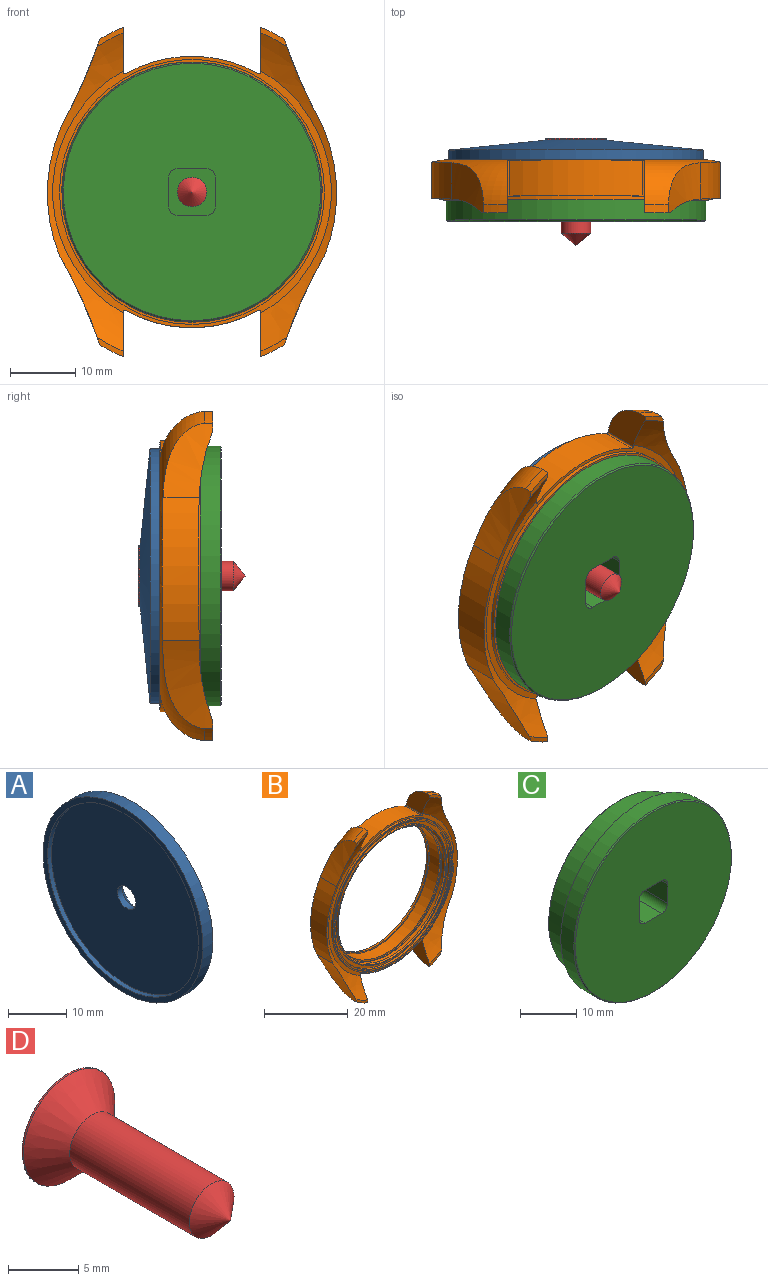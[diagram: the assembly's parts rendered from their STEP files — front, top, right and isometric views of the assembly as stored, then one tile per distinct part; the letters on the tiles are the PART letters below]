
ASSEMBLY  parts=4 mates=3
PART A: 7 faces, bbox 4x38.9x38.9 mm
  f0: cone r=19.47mm half-angle=84.2deg, axis (-1,0,0), area 1141.1mm2, adj f1,f6
  f1: cylinder r=19.47mm len=38.95mm, axis (-1,0,0), area 297.3mm2, adj f0,f2
  f2: plane 38.95x38.95mm, normal (-1,0,0), area 130.5mm2, adj f1,f3
  f3: cylinder r=18.38mm len=36.75mm, axis (-1,0,0), area 107.4mm2, adj f2,f4
  f4: plane 36.75x36.75mm, normal (-1,0,0), area 1044.8mm2, adj f3,f5
  f5: cylinder r=2.25mm len=4.5mm, axis (-1,0,0), area 17.6mm2, adj f4,f6
  f6: bspline ~8.47x8.47mm, area 54.6mm2, adj f0,f5
PART B: 52 faces, bbox 59.5x8.5x59.5 mm
  f0: cylinder r=27.3mm len=3.62mm, axis (0,-1,0), area 5mm2, adj f6,f9,f38,f46
  f1: cylinder r=27.3mm len=3.62mm, axis (0,-1,0), area 5mm2, adj f9,f35,f41,f44
  f2: plane 4x2.97mm, normal (0,-1,0), area 3.3mm2, adj f5,f7,f39,f45
  f3: plane 4x2.97mm, normal (0,-1,0), area 3.3mm2, adj f8,f34,f36,f43
  f4: plane 42.6x41.5mm, normal (0,-1,0), area 113mm2, adj f5,f33,f34,f36,f37,f38,f39,f40
  f5: torus R=10.97mm, axis (0,-1,0), area 113mm2, adj f2,f4,f6,f38,f39,f45,f46,f47
  f6: plane 4x2.97mm, normal (0,-1,0), area 3.3mm2, adj f0,f5,f38,f46
  f7: cylinder r=27.3mm len=3.62mm, axis (0,-1,0), area 5mm2, adj f2,f9,f39,f45
  f8: cylinder r=27.3mm len=3.62mm, axis (0,-1,0), area 5mm2, adj f3,f9,f36,f43
  f9: torus R=19.83mm, axis (0,-1,0), area 417.3mm2, adj f0,f1,f7,f8,f10,f36,f37,f38
  f10: plane 40.38x40.38mm, normal (0,1,0), area 90.5mm2, adj f9,f11
  f11: cylinder r=19.46mm len=38.93mm, axis (0,-1,0), area 137.6mm2, adj f10,f12
  f12: plane 38.93x38.93mm, normal (0,1,0), area 92.9mm2, adj f11,f13
  f13: cylinder r=18.69mm len=37.38mm, axis (0,-1,0), area 23.5mm2, adj f12,f14
  f14: plane 37.38x37.38mm, normal (0,1,0), area 49.2mm2, adj f13,f15
  f15: cone r=18.35mm half-angle=30deg, axis (0,1,0), area 19.9mm2, adj f14,f16
  f16: cylinder r=18.35mm len=36.7mm, axis (0,-1,0), area 89.4mm2, adj f15,f17
  f17: plane 36.7x36.7mm, normal (0,1,0), area 94.9mm2, adj f16,f18
  f18: cylinder r=17.51mm len=35.02mm, axis (0,-1,0), area 66mm2, adj f17,f19
  f19: plane 35.72x35.72mm, normal (0,-1,0), area 38.9mm2, adj f18,f20
  f20: cylinder r=17.86mm len=35.72mm, axis (0,-1,0), area 387.1mm2, adj f19,f21
  f21: plane 36.6x36.6mm, normal (0,-1,0), area 50.3mm2, adj f20,f22
  f22: cylinder r=18.3mm len=36.6mm, axis (0,-1,0), area 34.5mm2, adj f21,f23
  f23: cone r=18.3mm half-angle=43.3deg, axis (0,1,0), area 47.9mm2, adj f22,f24
  f24: cylinder r=18.01mm len=36.03mm, axis (0,-1,0), area 100.6mm2, adj f23,f25
  f25: cone r=18.3mm half-angle=43.3deg, axis (0,-1,0), area 47.9mm2, adj f24,f26
  f26: plane 37.03x37.03mm, normal (0,-1,0), area 24.6mm2, adj f25,f27
  f27: cylinder r=18.51mm len=37.03mm, axis (0,-1,0), area 65.7mm2, adj f26,f28
  f28: plane 39x39mm, normal (0,-1,0), area 117.6mm2, adj f27,f29
  f29: cylinder r=19.5mm len=39mm, axis (0,-1,0), area 75.3mm2, adj f28,f30
  f30: plane 39.83x39.83mm, normal (0,-1,0), area 51.4mm2, adj f29,f31
  f31: cylinder r=19.91mm len=39.83mm, axis (0,-1,0), area 31.3mm2, adj f30,f32
  f32: plane 40.5x40.5mm, normal (0,-1,0), area 42.6mm2, adj f31,f33
  f33: cylinder r=20.25mm len=40.5mm, axis (0,-1,0), area 76.3mm2, adj f4,f32
  f34: torus R=10.97mm, axis (0,-1,0), area 113mm2, adj f3,f4,f35,f36,f41,f42,f43,f44
  f35: plane 4x2.97mm, normal (0,-1,0), area 3.3mm2, adj f1,f34,f41,f44
  f36: plane 8.38x7.32mm, normal (-1,0,0), area 34.6mm2, adj f3,f4,f8,f9,f34,f48
  f37: cylinder r=20.75mm len=20.4mm, axis (0,1,0), area 117.4mm2, adj f4,f9,f48,f49
  f38: plane 8.38x7.32mm, normal (1,0,0), area 34.6mm2, adj f0,f4,f5,f6,f9,f49
  f39: plane 8.38x7.32mm, normal (1,0,0), area 34.6mm2, adj f2,f4,f5,f7,f9,f51
  f40: cylinder r=20.75mm len=20.4mm, axis (0,1,0), area 117.4mm2, adj f4,f9,f50,f51
  f41: plane 8.38x7.32mm, normal (-1,0,0), area 34.6mm2, adj f1,f4,f9,f34,f35,f50
  f42: cylinder r=25.39mm len=21.88mm, axis (0,1,0), area 125.6mm2, adj f9,f34,f43,f44
  f43: cylinder r=67.35mm len=13.52mm, axis (0,1,0), area 76.4mm2, adj f3,f8,f9,f34,f42
  f44: cylinder r=67.35mm len=11.33mm, axis (0,1,0), area 62.4mm2, adj f1,f9,f34,f35,f42
  f45: cylinder r=67.35mm len=11.33mm, axis (0,1,0), area 62.4mm2, adj f2,f5,f7,f9,f47
  f46: cylinder r=67.35mm len=13.52mm, axis (0,1,0), area 76.4mm2, adj f0,f5,f6,f9,f47
  f47: cylinder r=25.39mm len=21.88mm, axis (0,1,0), area 125.6mm2, adj f5,f9,f45,f46
  f48: cylinder r=0.2mm len=5.5mm, axis (0,1,0), area 2.3mm2, adj f4,f9,f36,f37
  f49: cylinder r=0.2mm len=5.5mm, axis (0,1,0), area 2.3mm2, adj f4,f9,f37,f38
  f50: cylinder r=0.2mm len=5.5mm, axis (0,1,0), area 2.3mm2, adj f4,f9,f40,f41
  f51: cylinder r=0.2mm len=5.5mm, axis (0,1,0), area 2.3mm2, adj f4,f9,f39,f40
PART C: 17 faces, bbox 39.8x8.8x39.8 mm
  f0: plane 39.35x39.35mm, normal (0,-1,0), area 1166.2mm2, adj f6,f7,f8,f9,f10,f11,f12,f13
  f1: cylinder r=2.25mm len=4.5mm, axis (0,1,0), area 25.4mm2, adj f4,f14
  f2: plane 39.75x39.75mm, normal (0,1,0), area 242.8mm2, adj f3,f5
  f3: cylinder r=17.82mm len=35.65mm, axis (0,-1,0), area 571.2mm2, adj f2,f15
  f4: plane 35.25x35.25mm, normal (0,1,0), area 960mm2, adj f1,f15
  f5: cylinder r=19.88mm len=39.75mm, axis (0,-1,0), area 412.1mm2, adj f2,f16
  f6: plane 7x4.2mm, normal (0,0,1), area 29.4mm2, adj f0,f7,f13,f14
  f7: cylinder r=1.5mm len=7mm, axis (0,-1,0), area 16.5mm2, adj f0,f6,f8,f14
  f8: plane 7x4.2mm, normal (-1,0,0), area 29.4mm2, adj f0,f7,f9,f14
  f9: cylinder r=1.5mm len=7mm, axis (0,-1,0), area 16.5mm2, adj f0,f8,f10,f14
  f10: plane 7x4.2mm, normal (0,0,-1), area 29.4mm2, adj f0,f9,f11,f14
  f11: cylinder r=1.5mm len=7mm, axis (0,-1,0), area 16.5mm2, adj f0,f10,f12,f14
  f12: plane 7x4.2mm, normal (1,0,0), area 29.4mm2, adj f0,f11,f13,f14
  f13: cylinder r=1.5mm len=7mm, axis (0,-1,0), area 16.5mm2, adj f0,f6,f12,f14
  f14: plane 7.2x7.2mm, normal (0,-1,0), area 34mm2, adj f1,f6,f7,f8,f9,f10,f11,f12
  f15: cone r=17.82mm half-angle=45deg, axis (0,-1,0), area 31.5mm2, adj f3,f4
  f16: cone r=19.68mm half-angle=45deg, axis (0,1,0), area 35.1mm2, adj f0,f5
PART D: 18 faces, bbox 10x16.4x10 mm
  f0: cylinder r=2.25mm len=12mm, axis (0,-1,0), area 169.6mm2, adj f1,f3
  f1: cone r=2.25mm half-angle=45deg, axis (0,1,0), area 70.7mm2, adj f0,f17
  f2: plane 9.02x9.02mm, normal (0,1,0), area 50.3mm2, adj f4,f5,f6,f7,f8,f9,f11,f12
  f3: cone r=2.25mm half-angle=50deg, axis (0,1,0), area 20.8mm2, adj f0
  f4: plane 2.05x1.5mm, normal (-0.01,0,1), area 3.1mm2, adj f2,f10,f11,f16
  f5: plane 1.76x1.5mm, normal (0.86,0,0.51), area 3.1mm2, adj f2,f10,f11,f12
  f6: plane 1.79x1.5mm, normal (0.87,0,-0.49), area 3.1mm2, adj f2,f10,f12,f13
  f7: plane 2.05x1.5mm, normal (0.01,0,-1), area 3.1mm2, adj f2,f10,f13,f14
  f8: plane 1.76x1.5mm, normal (-0.86,0,-0.51), area 3.1mm2, adj f2,f10,f14,f15
  f9: plane 1.79x1.5mm, normal (-0.87,0,0.49), area 3.1mm2, adj f2,f10,f15,f16
  f10: plane 4.51x3.99mm, normal (0,1,0), area 13.5mm2, adj f4,f5,f6,f7,f8,f9,f11,f12
  f11: cylinder r=0.2mm len=1.5mm, axis (0,-1,0), area 0.3mm2, adj f2,f4,f5,f10
  f12: cylinder r=0.2mm len=1.5mm, axis (0,-1,0), area 0.3mm2, adj f2,f5,f6,f10
  f13: cylinder r=0.2mm len=1.5mm, axis (0,-1,0), area 0.3mm2, adj f2,f6,f7,f10
  f14: cylinder r=0.2mm len=1.5mm, axis (0,-1,0), area 0.3mm2, adj f2,f7,f8,f10
  f15: cylinder r=0.2mm len=1.5mm, axis (0,-1,0), area 0.3mm2, adj f2,f8,f9,f10
  f16: cylinder r=0.2mm len=1.5mm, axis (0,-1,0), area 0.3mm2, adj f2,f4,f9,f10
  f17: torus R=4.51mm, axis (0,-1,0), area 6.8mm2, adj f1,f2
PLACE A rot(axis=(0,0,1),90deg) t=(-18.49,-8.27,-2.25)mm
PLACE B t=(-0.93,-13.29,-2.25)mm
PLACE C t=(-18.44,-13.04,-2.25)mm fixed
PLACE D t=(-18.44,-21.36,-2.25)mm
MATE fastened C.f3 <-> B.f0  axis (0,1,0) through (-18.44,-7.74,-2.25)mm
MATE fastened A.f0 <-> D.f0  axis (0,-1,0) through (-18.44,-4.86,-2.25)mm
MATE fastened B.f0 <-> A.f0  axis (0,1,0) through (-18.44,-8.07,-2.25)mm
